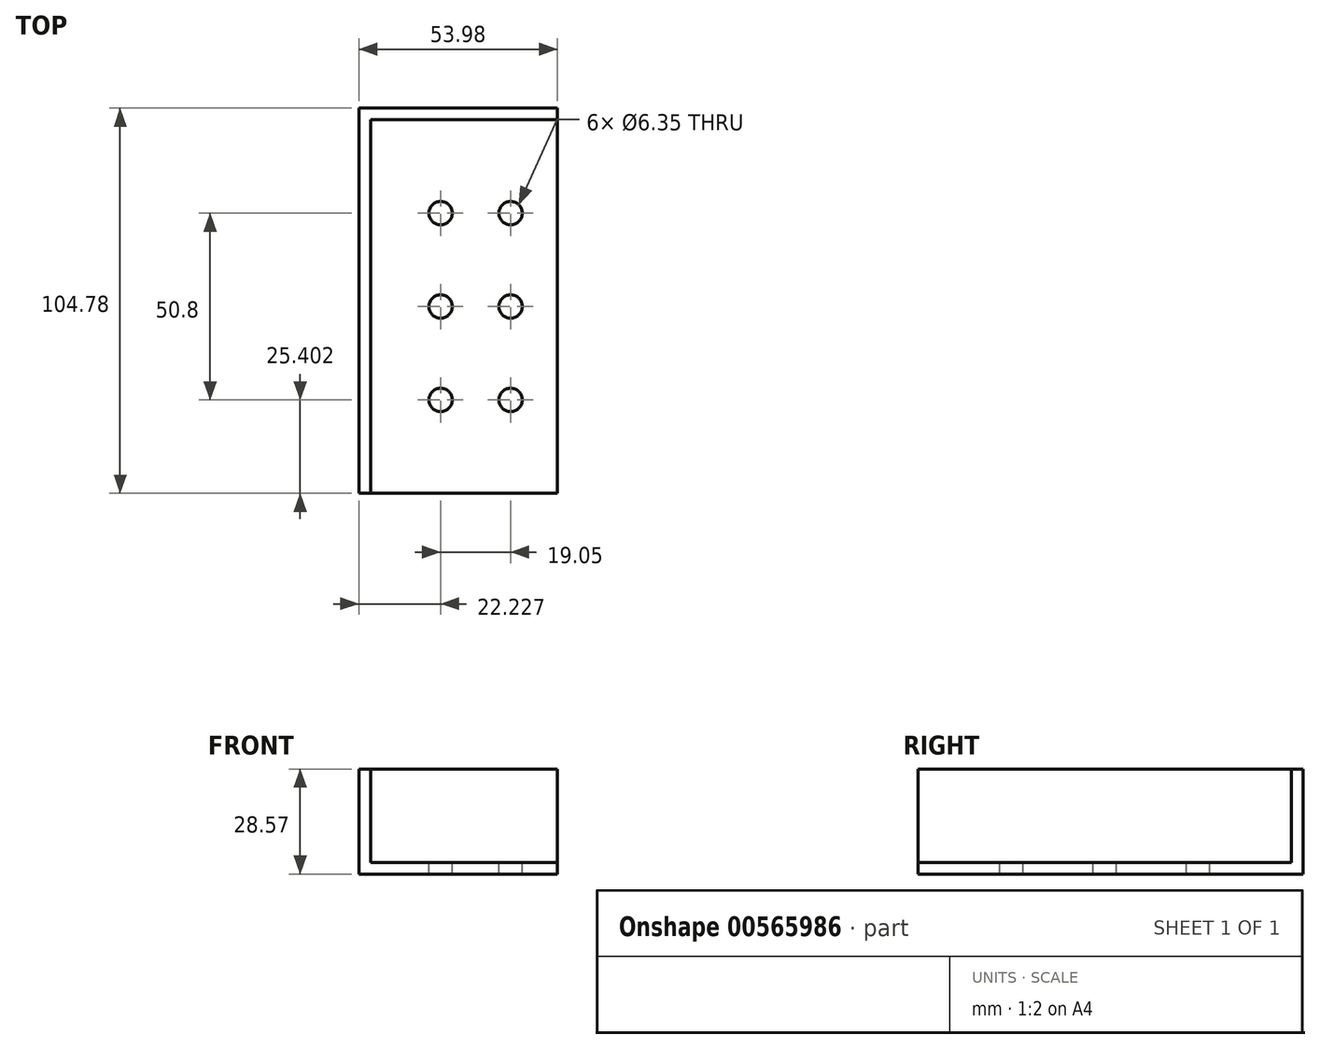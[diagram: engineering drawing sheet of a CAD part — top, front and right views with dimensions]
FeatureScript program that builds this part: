
annotation { "Feature Type Name" : "Feature", "Feature Type Description" : "" }
export const myFeature = defineFeature(function(context is Context, id is Id, definition is map)
    precondition{}
    {
        {
            var Q0;
            Q0=qCreatedBy(makeId("Top.planeOp"),FACE);
            var sketch = newSketch(context, id + "F0", { "sketchPlane" : qUnion([Q0])});
            skLineSegment(sketch, "E0.bottom", {"start": v(-26.99, 52.39) * mm, "end": v(26.99, 52.39) * mm});
            skLineSegment(sketch, "E0.top", {"start": v(-26.99, -52.39) * mm, "end": v(26.99, -52.39) * mm});
            skLineSegment(sketch, "E0.left", {"start": v(-26.99, 52.39) * mm, "end": v(-26.99, -52.39) * mm});
            skLineSegment(sketch, "E0.right", {"start": v(26.99, 52.39) * mm, "end": v(26.99, -52.39) * mm});
            skPoint(sketch, "E0.middle", {"position": v(0, 0) * mm});
            skSolve(sketch);
        }
        {
            var Q0;
            Q0=makeQuery(id+"F0.imprint","IMPRINT",FACE,{"disambiguationData":[TD([[makeQuery(id+"F0.imprint","IMPRINT",EDGE,{"derivedFrom":sQuery(id+"F0.wireOp",EDGE,"E0.bottom")}),-1.0]])]});
            extrude(context, id + "F1", {"entities" : qUnion([Q0]), "depth" : 3.17 * mm, "offsetDistance" : 25.4 * mm});
        }
        {
            var Q0;
            Q0=makeQuery(id+"F1.opExtrude","CAP_FACE",FACE,{"disambiguationData":[OSD([sQuery(id+"F0.wireOp",EDGE,"E0.bottom"),sQuery(id+"F0.wireOp",EDGE,"E0.top"),sQuery(id+"F0.wireOp",EDGE,"E0.left"),sQuery(id+"F0.wireOp",EDGE,"E0.right")])],"isStart":false});
            var sketch = newSketch(context, id + "F2", { "sketchPlane" : qUnion([Q0])});
            skCircle(sketch, "E1", {"center": v(14.29, 23.81) * mm, "radius": 3.18 * mm});
            skCircle(sketch, "E2", {"center": v(14.29, -26.99) * mm, "radius": 3.18 * mm});
            skCircle(sketch, "E3", {"center": v(-4.76, 23.81) * mm, "radius": 3.18 * mm});
            skCircle(sketch, "E4", {"center": v(-4.76, -26.99) * mm, "radius": 3.18 * mm});
            skCircle(sketch, "E5", {"center": v(-4.76, -1.59) * mm, "radius": 3.18 * mm});
            skCircle(sketch, "E6", {"center": v(14.29, -1.59) * mm, "radius": 3.18 * mm});
            skSolve(sketch);
        }
        {
            var Q0;
            Q0=makeQuery(id+"F1.opExtrude","CAP_FACE",FACE,{"disambiguationData":[OSD([sQuery(id+"F0.wireOp",EDGE,"E0.bottom"),sQuery(id+"F0.wireOp",EDGE,"E0.top"),sQuery(id+"F0.wireOp",EDGE,"E0.left"),sQuery(id+"F0.wireOp",EDGE,"E0.right")])],"isStart":false});
            var sketch = newSketch(context, id + "F3", { "sketchPlane" : qUnion([Q0])});
            skLineSegment(sketch, "E7", {"start": v(26.99, 49.21) * mm, "end": v(-26.99, 49.21) * mm});
            skLineSegment(sketch, "E8", {"start": v(-23.81, -52.39) * mm, "end": v(-23.81, 49.21) * mm});
            skSolve(sketch);
        }
        {
            var Q0;
            {var subQ1=makeQuery(id+"F1.opExtrude","CAP_EDGE",EDGE,{"disambiguationData":[OSD([sQuery(id+"F0.wireOp",EDGE,"E0.bottom")])],"isStart":false});Q0=makeQuery(id+"F3.imprint","IMPRINT",FACE,{"disambiguationData":[TD([[makeQuery(id+"F3.imprint","IMPRINT",EDGE,{"derivedFrom":subQ1}),-1.0]])]});}
            var Q1;
            {var subQ3=sQuery(id+"F3.wireOp",EDGE,"E8");Q1=makeQuery(id+"F3.imprint","IMPRINT",FACE,{"disambiguationData":[TD([[makeQuery(id+"F3.imprint","IMPRINT",EDGE,{"derivedFrom":subQ3}),1.0]])]});}
            extrude(context, id + "F4", {"entities" : qUnion([Q0, Q1]), "operationType" : NewBodyOperationType.ADD, "depth" : 25.4 * mm, "offsetDistance" : 25.4 * mm});
        }
        {
            var Q0;
            Q0=makeQuery(id+"F2.imprint","IMPRINT",FACE,{"disambiguationData":[TD([[makeQuery(id+"F2.imprint","IMPRINT",EDGE,{"derivedFrom":sQuery(id+"F2.wireOp",EDGE,"E3")}),1.0]])]});
            var Q1;
            Q1=makeQuery(id+"F2.imprint","IMPRINT",FACE,{"disambiguationData":[TD([[makeQuery(id+"F2.imprint","IMPRINT",EDGE,{"derivedFrom":sQuery(id+"F2.wireOp",EDGE,"E1")}),1.0]])]});
            var Q2;
            Q2=makeQuery(id+"F2.imprint","IMPRINT",FACE,{"disambiguationData":[TD([[makeQuery(id+"F2.imprint","IMPRINT",EDGE,{"derivedFrom":sQuery(id+"F2.wireOp",EDGE,"E5")}),1.0]])]});
            var Q3;
            Q3=makeQuery(id+"F2.imprint","IMPRINT",FACE,{"disambiguationData":[TD([[makeQuery(id+"F2.imprint","IMPRINT",EDGE,{"derivedFrom":sQuery(id+"F2.wireOp",EDGE,"E6")}),1.0]])]});
            var Q4;
            Q4=makeQuery(id+"F2.imprint","IMPRINT",FACE,{"disambiguationData":[TD([[makeQuery(id+"F2.imprint","IMPRINT",EDGE,{"derivedFrom":sQuery(id+"F2.wireOp",EDGE,"E4")}),1.0]])]});
            var Q5;
            Q5=makeQuery(id+"F2.imprint","IMPRINT",FACE,{"disambiguationData":[TD([[makeQuery(id+"F2.imprint","IMPRINT",EDGE,{"derivedFrom":sQuery(id+"F2.wireOp",EDGE,"E2")}),1.0]])]});
            extrude(context, id + "F5", {"entities" : qUnion([Q0, Q1, Q2, Q3, Q4, Q5]), "operationType" : NewBodyOperationType.REMOVE, "oppositeDirection" : true, "depth" : 25.4 * mm, "offsetDistance" : 25.4 * mm});
        }
    });
